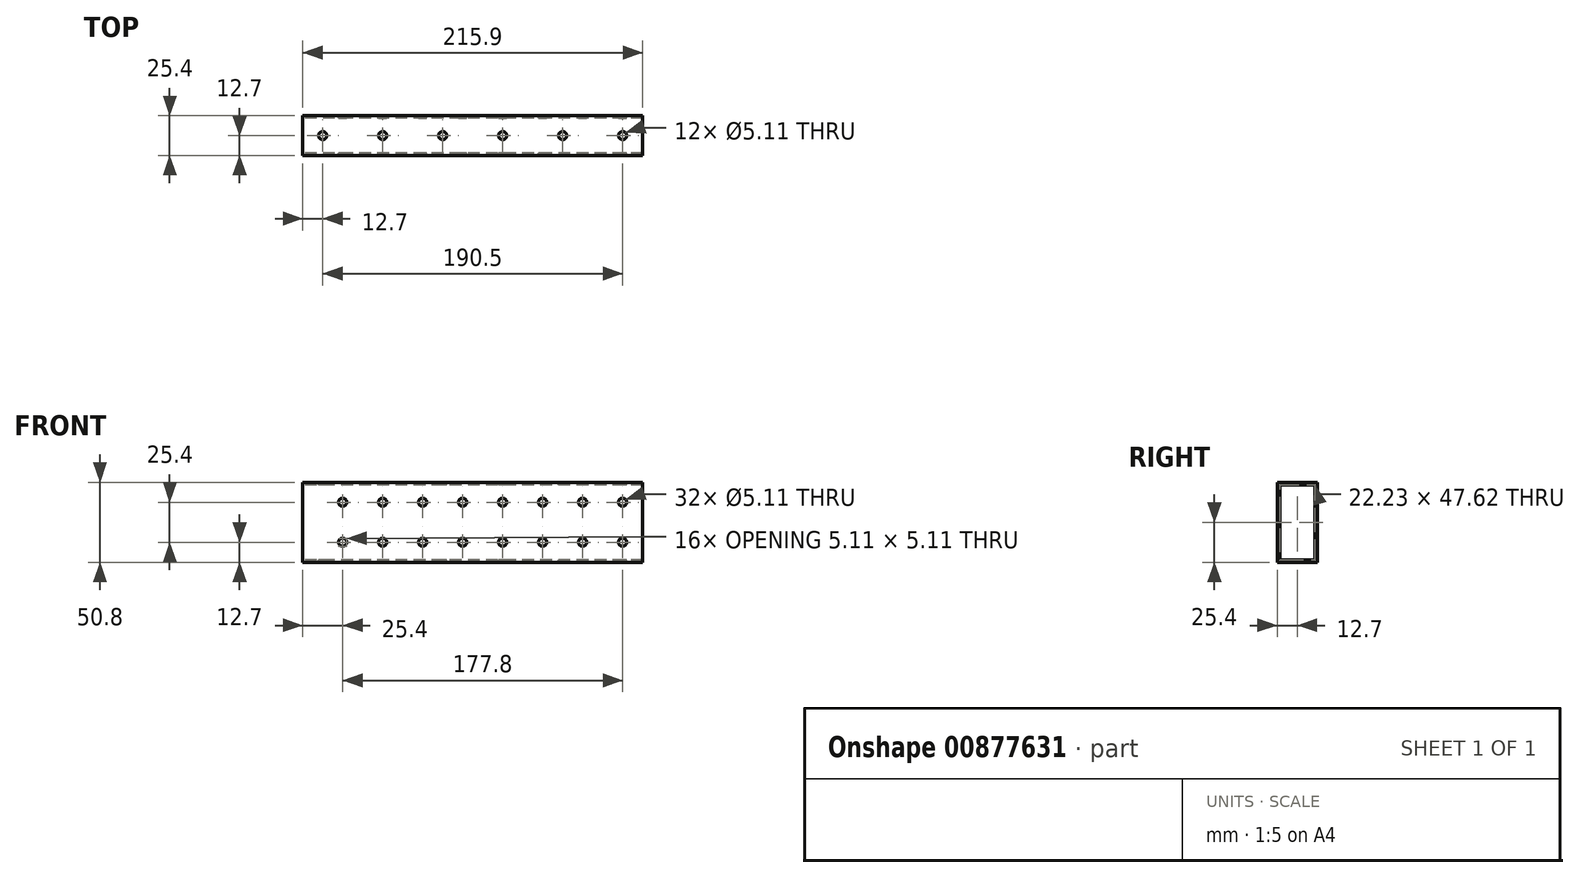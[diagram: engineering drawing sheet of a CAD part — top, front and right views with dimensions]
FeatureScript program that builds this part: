
annotation { "Feature Type Name" : "Feature", "Feature Type Description" : "" }
export const myFeature = defineFeature(function(context is Context, id is Id, definition is map)
    precondition{}
    {
        {
            var Q0;
            Q0=qCreatedBy(makeId("Front.planeOp"),FACE);
            var sketch = newSketch(context, id + "F0", { "sketchPlane" : qUnion([Q0])});
            skLineSegment(sketch, "E0.bottom", {"start": v(-107.95, 25.4) * mm, "end": v(107.95, 25.4) * mm});
            skLineSegment(sketch, "E0.top", {"start": v(-107.95, -25.4) * mm, "end": v(107.95, -25.4) * mm});
            skLineSegment(sketch, "E0.left", {"start": v(-107.95, 25.4) * mm, "end": v(-107.95, -25.4) * mm});
            skLineSegment(sketch, "E0.right", {"start": v(107.95, 25.4) * mm, "end": v(107.95, -25.4) * mm});
            skPoint(sketch, "E0.middle", {"position": v(0, 0) * mm});
            skCircle(sketch, "E1", {"center": v(95.25, 12.7) * mm, "radius": 2.55 * mm});
            skCircle(sketch, "E2.0.1.0", {"center": v(95.25, -12.7) * mm, "radius": 2.55 * mm});
            skCircle(sketch, "E2.1.0.0", {"center": v(69.85, 12.7) * mm, "radius": 2.55 * mm});
            skCircle(sketch, "E2.1.1.0", {"center": v(69.85, -12.7) * mm, "radius": 2.55 * mm});
            skCircle(sketch, "E2.2.0.0", {"center": v(44.45, 12.7) * mm, "radius": 2.55 * mm});
            skCircle(sketch, "E2.2.1.0", {"center": v(44.45, -12.7) * mm, "radius": 2.55 * mm});
            skCircle(sketch, "E2.3.0.0", {"center": v(19.05, 12.7) * mm, "radius": 2.55 * mm});
            skCircle(sketch, "E2.3.1.0", {"center": v(19.05, -12.7) * mm, "radius": 2.55 * mm});
            skCircle(sketch, "E2.4.0.0", {"center": v(-6.35, 12.7) * mm, "radius": 2.55 * mm});
            skCircle(sketch, "E2.4.1.0", {"center": v(-6.35, -12.7) * mm, "radius": 2.55 * mm});
            skCircle(sketch, "E2.5.0.0", {"center": v(-31.75, 12.7) * mm, "radius": 2.55 * mm});
            skCircle(sketch, "E2.5.1.0", {"center": v(-31.75, -12.7) * mm, "radius": 2.55 * mm});
            skCircle(sketch, "E2.6.0.0", {"center": v(-57.15, 12.7) * mm, "radius": 2.55 * mm});
            skCircle(sketch, "E2.6.1.0", {"center": v(-57.15, -12.7) * mm, "radius": 2.55 * mm});
            skLineSegment(sketch, "E2.direction1", {"start": v(95.25, 12.7) * mm, "end": v(69.85, 12.7) * mm, "construction": true});
            skLineSegment(sketch, "E2.direction2", {"start": v(95.25, 12.7) * mm, "end": v(95.25, -12.7) * mm, "construction": true});
            skCircle(sketch, "E3.0.7.0", {"center": v(-82.55, 12.7) * mm, "radius": 2.55 * mm});
            skCircle(sketch, "E3.0.7.1", {"center": v(-82.55, -12.7) * mm, "radius": 2.55 * mm});
            skSolve(sketch);
        }
        {
            var Q0;
            Q0=qSketchRegion(id+"F0",true);
            extrude(context, id + "F1", {"entities" : qUnion([Q0]), "depth" : 25.4 * mm, "offsetDistance" : 25.4 * mm});
        }
        {
            var Q0;
            Q0=makeQuery(id+"F1.opExtrude","SWEPT_FACE",FACE,{"disambiguationData":[OSD([sQuery(id+"F0.wireOp",EDGE,"E0.left")])]});
            var sketch = newSketch(context, id + "F2", { "sketchPlane" : qUnion([Q0])});
            skLineSegment(sketch, "E4.bottom", {"start": v(23.81, 23.81) * mm, "end": v(1.59, 23.81) * mm});
            skLineSegment(sketch, "E4.top", {"start": v(23.81, -23.81) * mm, "end": v(1.59, -23.81) * mm});
            skLineSegment(sketch, "E4.left", {"start": v(23.81, 23.81) * mm, "end": v(23.81, -23.81) * mm});
            skLineSegment(sketch, "E4.right", {"start": v(1.59, 23.81) * mm, "end": v(1.59, -23.81) * mm});
            skPoint(sketch, "E4.middle", {"position": v(12.7, 0) * mm});
            skPoint(sketch, "E4.middle.positionSnap0", {"position": v(12.7, 25.4) * mm});
            skPoint(sketch, "E4.centerSnap0", {"position": v(12.7, 25.4) * mm});
            skSolve(sketch);
        }
        {
            var Q0;
            Q0=qSketchRegion(id+"F2",true);
            extrude(context, id + "F3", {"entities" : qUnion([Q0]), "operationType" : NewBodyOperationType.REMOVE, "endBound" : BoundingType.THROUGH_ALL, "oppositeDirection" : true, "depth" : 25.4 * mm, "offsetDistance" : 25.4 * mm});
        }
        {
            var Q0;
            Q0=makeQuery(id+"F1.opExtrude","SWEPT_FACE",FACE,{"disambiguationData":[OSD([sQuery(id+"F0.wireOp",EDGE,"E0.bottom")])]});
            var sketch = newSketch(context, id + "F4", { "sketchPlane" : qUnion([Q0])});
            skCircle(sketch, "E5", {"center": v(-95.25, -12.7) * mm, "radius": 2.55 * mm});
            skPoint(sketch, "E5.centerSnap0", {"position": v(-107.95, -12.7) * mm});
            skCircle(sketch, "E6.1.0.0", {"center": v(-57.15, -12.7) * mm, "radius": 2.55 * mm});
            skCircle(sketch, "E6.2.0.0", {"center": v(-19.05, -12.7) * mm, "radius": 2.55 * mm});
            skCircle(sketch, "E6.3.0.0", {"center": v(19.05, -12.7) * mm, "radius": 2.55 * mm});
            skCircle(sketch, "E6.4.0.0", {"center": v(57.15, -12.7) * mm, "radius": 2.55 * mm});
            skCircle(sketch, "E6.5.0.0", {"center": v(95.25, -12.7) * mm, "radius": 2.55 * mm});
            skLineSegment(sketch, "E6.direction1", {"start": v(-95.25, -12.7) * mm, "end": v(-57.15, -12.7) * mm, "construction": true});
            skSolve(sketch);
        }
        {
            var Q0;
            Q0=qSketchRegion(id+"F4",true);
            extrude(context, id + "F5", {"entities" : qUnion([Q0]), "operationType" : NewBodyOperationType.REMOVE, "endBound" : BoundingType.THROUGH_ALL, "oppositeDirection" : true, "depth" : 25.4 * mm, "offsetDistance" : 25.4 * mm});
        }
    });
